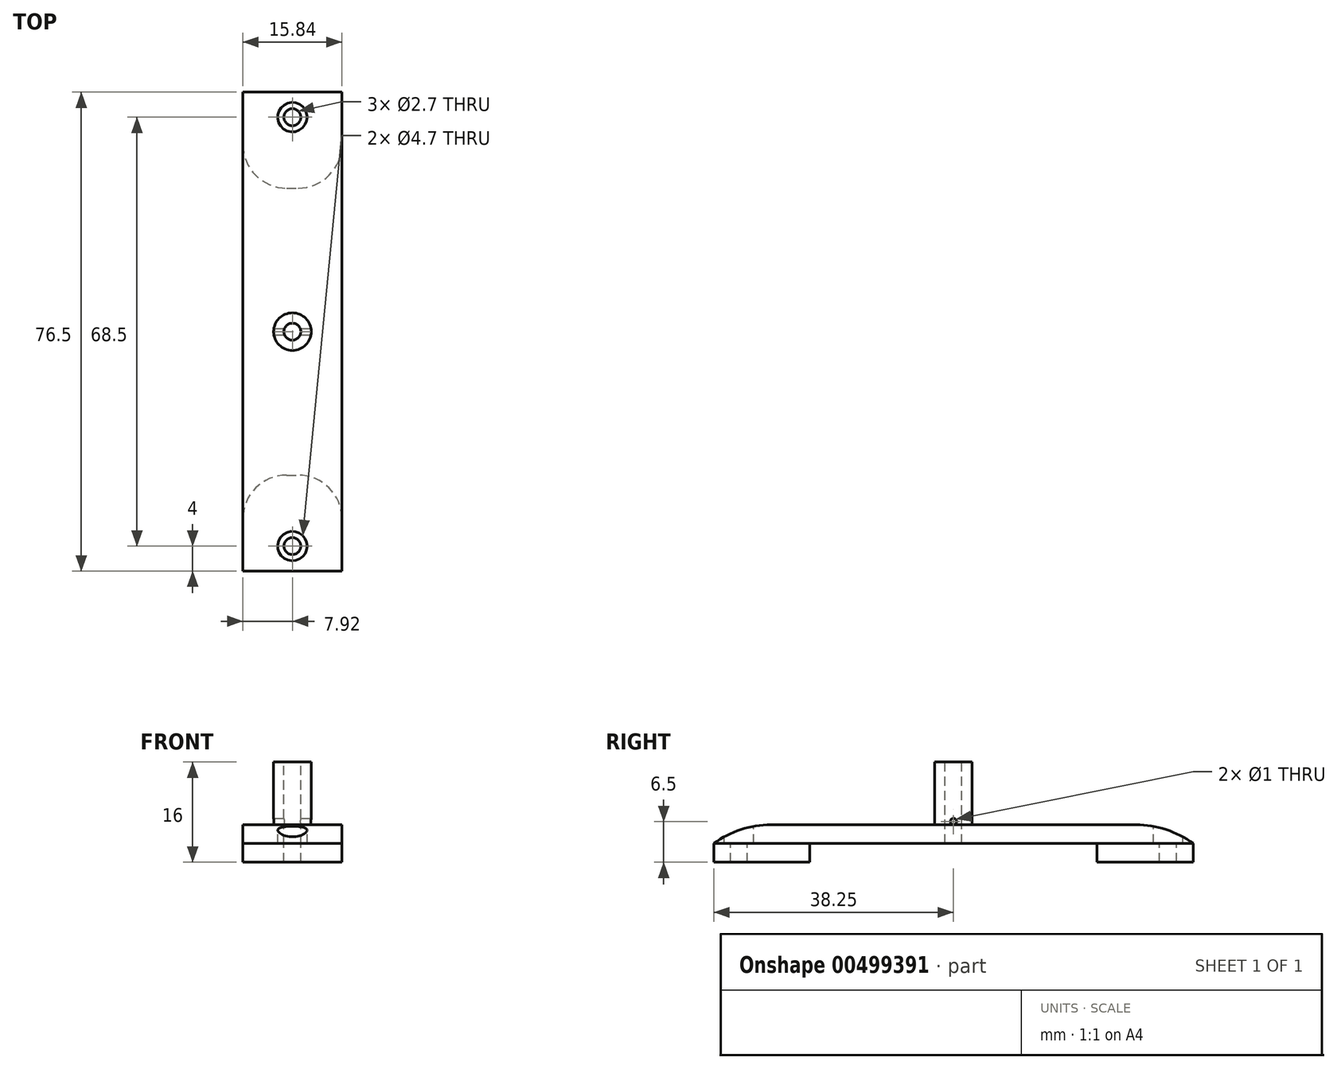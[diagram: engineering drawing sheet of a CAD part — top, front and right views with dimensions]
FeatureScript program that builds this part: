
annotation { "Feature Type Name" : "Feature", "Feature Type Description" : "" }
export const myFeature = defineFeature(function(context is Context, id is Id, definition is map)
    precondition{}
    {
        {
            var Q0;
            Q0=qCreatedBy(makeId("Top.planeOp"),FACE);
            var sketch = newSketch(context, id + "F0", { "sketchPlane" : qUnion([Q0])});
            skLineSegment(sketch, "E0.bottom", {"start": v(-7.92, 38.25) * mm, "end": v(7.91, 38.25) * mm});
            skLineSegment(sketch, "E0.top", {"start": v(-7.92, 22.92) * mm, "end": v(7.91, 22.92) * mm});
            skLineSegment(sketch, "E0.left", {"start": v(-7.92, 22.92) * mm, "end": v(-7.92, 38.25) * mm});
            skLineSegment(sketch, "E0.right", {"start": v(7.91, 22.92) * mm, "end": v(7.91, 38.25) * mm});
            skPoint(sketch, "E0.middle", {"position": v(0, 30.59) * mm});
            skLineSegment(sketch, "E1.bottom", {"start": v(-7.92, -38.25) * mm, "end": v(7.91, -38.25) * mm});
            skLineSegment(sketch, "E1.top", {"start": v(-7.92, -22.92) * mm, "end": v(7.91, -22.92) * mm});
            skLineSegment(sketch, "E1.left", {"start": v(-7.91, -38.25) * mm, "end": v(-7.91, -22.92) * mm});
            skLineSegment(sketch, "E1.right", {"start": v(7.92, -38.25) * mm, "end": v(7.92, -22.92) * mm});
            skPoint(sketch, "E1.middle", {"position": v(0, -30.58) * mm});
            skSolve(sketch);
        }
        {
            var Q0;
            Q0=makeQuery(id+"F0.imprint","IMPRINT",FACE,{"disambiguationData":[TD([[makeQuery(id+"F0.imprint","IMPRINT",EDGE,{"derivedFrom":sQuery(id+"F0.wireOp",EDGE,"E0.bottom")}),-1.0]])]});
            var Q1;
            Q1=makeQuery(id+"F0.imprint","IMPRINT",FACE,{"disambiguationData":[TD([[makeQuery(id+"F0.imprint","IMPRINT",EDGE,{"derivedFrom":sQuery(id+"F0.wireOp",EDGE,"E1.bottom")}),1.0]])]});
            extrude(context, id + "F1", {"entities" : qUnion([Q0, Q1]), "depth" : 3 * mm});
        }
        {
            var Q0;
            Q0=makeQuery(id+"F1.opExtrude","SWEPT_EDGE",EDGE,{"disambiguationData":[OSD([sQuery(id+"F0.wireOp",EDGE,"E0.top"),sQuery(id+"F0.wireOp",EDGE,"E0.left")])]});
            var Q1;
            Q1=makeQuery(id+"F1.opExtrude","SWEPT_EDGE",EDGE,{"disambiguationData":[OSD([sQuery(id+"F0.wireOp",EDGE,"E0.top"),sQuery(id+"F0.wireOp",EDGE,"E0.right")])]});
            var Q2;
            Q2=makeQuery(id+"F1.opExtrude","SWEPT_EDGE",EDGE,{"disambiguationData":[OSD([sQuery(id+"F0.wireOp",EDGE,"E1.top"),sQuery(id+"F0.wireOp",EDGE,"E1.left")])]});
            var Q3;
            Q3=makeQuery(id+"F1.opExtrude","SWEPT_EDGE",EDGE,{"disambiguationData":[OSD([sQuery(id+"F0.wireOp",EDGE,"E1.top"),sQuery(id+"F0.wireOp",EDGE,"E1.right")])]});
            fillet(context, id + "F2", {"entities" : qUnion([Q0, Q1, Q2, Q3]), "radius" : 7 * mm, "tangentPropagation" : true, "allowEdgeOverflow" : false});
        }
        {
            var Q0;
            Q0=makeQuery(id+"F1.opExtrude","CAP_EDGE",EDGE,{"disambiguationData":[OSD([sQuery(id+"F0.wireOp",EDGE,"E1.bottom")])],"isStart":false});
            cPoint(context, id + "F3", {"entities" : qUnion([Q0]), "parameter" : 0.5});
        }
        {
            var Q0;
            Q0=makeQuery(id+"F1.opExtrude","CAP_EDGE",EDGE,{"disambiguationData":[OSD([sQuery(id+"F0.wireOp",EDGE,"E0.bottom")])],"isStart":false});
            var Q1;
            Q1 = qCreatedBy(id + "F3" ,VERTEX);
            cPlane(context, id + "F4", {"entities" : qUnion([Q0, Q1]), "cplaneType" : CPlaneType.LINE_ANGLE, "offset" : 25 * mm, "angle" : 0 * degree, "width" : 150 * mm, "height" : 150 * mm});
        }
        {
            var Q0;
            Q0=qCreatedBy(id+"F4.planeOp",FACE);
            var sketch = newSketch(context, id + "F5", { "sketchPlane" : qUnion([Q0])});
            skLineSegment(sketch, "E2.bottom", {"start": v(-7.91, 38.25) * mm, "end": v(7.92, 38.25) * mm});
            skLineSegment(sketch, "E2.top", {"start": v(-7.92, -38.25) * mm, "end": v(7.91, -38.25) * mm});
            skLineSegment(sketch, "E2.left", {"start": v(-7.91, 38.25) * mm, "end": v(-7.92, -38.25) * mm});
            skLineSegment(sketch, "E2.right", {"start": v(7.92, 38.25) * mm, "end": v(7.91, -38.25) * mm});
            skPoint(sketch, "E2.middle", {"position": v(0, 0) * mm});
            skSolve(sketch);
        }
        {
            var Q0;
            Q0 = qSketchRegion(id + "F5", true);
            extrude(context, id + "F6", {"entities" : qUnion([Q0]), "oppositeDirection" : true, "depth" : 3 * mm});
        }
        {
            var Q0;
            Q0=makeQuery(id+"F6.opExtrude","CAP_EDGE",EDGE,{"disambiguationData":[OSD([sQuery(id+"F5.wireOp",EDGE,"E2.top")])],"isStart":false});
            var Q1;
            Q1=makeQuery(id+"F6.opExtrude","CAP_EDGE",EDGE,{"disambiguationData":[OSD([sQuery(id+"F5.wireOp",EDGE,"E2.bottom")])],"isStart":false});
            fillet(context, id + "F7", {"entities" : qUnion([Q0, Q1]), "radius" : 15.36 * mm, "allowEdgeOverflow" : false});
        }
        {
            var Q0;
            Q0=makeQuery(id+"F6.opExtrude","CAP_EDGE",EDGE,{"disambiguationData":[OSD([sQuery(id+"F5.wireOp",EDGE,"E2.left")])],"isStart":false});
            cPoint(context, id + "F8", {"entities" : qUnion([Q0]), "parameter" : 0.5});
        }
        {
            var Q0;
            Q0=makeQuery(id+"F6.opExtrude","CAP_EDGE",EDGE,{"disambiguationData":[OSD([sQuery(id+"F5.wireOp",EDGE,"E2.right")])],"isStart":false});
            var Q1;
            Q1 = qCreatedBy(id + "F8" ,VERTEX);
            cPlane(context, id + "F9", {"entities" : qUnion([Q0, Q1]), "cplaneType" : CPlaneType.LINE_ANGLE, "offset" : 25 * mm, "angle" : 0 * degree, "width" : 150 * mm, "height" : 150 * mm});
        }
        {
            var Q0;
            Q0=qCreatedBy(id+"F9.planeOp",FACE);
            var sketch = newSketch(context, id + "F10", { "sketchPlane" : qUnion([Q0])});
            skCircle(sketch, "E3", {"center": v(0, 34.25) * mm, "radius": 1.5 * mm});
            skCircle(sketch, "E4", {"center": v(0, -34.25) * mm, "radius": 1.5 * mm});
            skSolve(sketch);
        }
        {
            var Q0;
            Q0=sQuery(id+"F10.wireOp",VERTEX,"E3.center");
            var Q1;
            Q1=sQuery(id+"F10.wireOp",VERTEX,"E4.center");
            var Q2;
            Q2=makeQuery(id+"F1.opExtrude","SWEPT_BODY",BODY,{"disambiguationData":[OSD([sQuery(id+"F0.wireOp",EDGE,"E0.bottom"),sQuery(id+"F0.wireOp",EDGE,"E0.top"),sQuery(id+"F0.wireOp",EDGE,"E0.left"),sQuery(id+"F0.wireOp",EDGE,"E0.right")])]});
            var Q3;
            Q3=makeQuery(id+"F6.opExtrude","SWEPT_BODY",BODY,{"disambiguationData":[OSD([sQuery(id+"F5.wireOp",EDGE,"E2.bottom"),sQuery(id+"F5.wireOp",EDGE,"E2.top"),sQuery(id+"F5.wireOp",EDGE,"E2.left"),sQuery(id+"F5.wireOp",EDGE,"E2.right")])]});
            var Q4;
            Q4=makeQuery(id+"F1.opExtrude","SWEPT_BODY",BODY,{"disambiguationData":[OSD([sQuery(id+"F0.wireOp",EDGE,"E1.bottom"),sQuery(id+"F0.wireOp",EDGE,"E1.top"),sQuery(id+"F0.wireOp",EDGE,"E1.left"),sQuery(id+"F0.wireOp",EDGE,"E1.right")])]});
            hole(context, id + "F11", {"style" : HoleStyle.C_BORE, "endStyle" : HoleEndStyle.BLIND, "holeDiameter" : 2.7 * mm, "cBoreDiameter" : 4.7 * mm, "cBoreDepth" : 3 * mm, "holeDepth" : 10 * mm, "isTappedThrough" : true, "tappedDepth" : 12 * mm, "tapClearance" : 3, "startFromSketch" : true, "locations" : qUnion([Q0, Q1]), "scope" : qUnion([Q2, Q3, Q4])});
        }
        {
            var Q0;
            Q0=qCreatedBy(id+"F9.planeOp",FACE);
            var sketch = newSketch(context, id + "F12", { "sketchPlane" : qUnion([Q0])});
            skCircle(sketch, "E5", {"center": v(0, 0) * mm, "radius": 3 * mm});
            skSolve(sketch);
        }
        {
            var Q0;
            Q0=makeQuery(id+"F12.imprint","IMPRINT",FACE,{"disambiguationData":[TD([[makeQuery(id+"F12.imprint","IMPRINT",EDGE,{"derivedFrom":sQuery(id+"F12.wireOp",EDGE,"E5")}),1.0]])]});
            extrude(context, id + "F13", {"entities" : qUnion([Q0]), "operationType" : NewBodyOperationType.ADD, "depth" : 10 * mm});
        }
        {
            var Q0;
            Q0=makeQuery(id+"F13.opExtrude","CAP_FACE",FACE,{"disambiguationData":[OSD([sQuery(id+"F12.wireOp",EDGE,"E5")])],"isStart":false});
            var sketch = newSketch(context, id + "F14", { "sketchPlane" : qUnion([Q0])});
            skCircle(sketch, "E6", {"center": v(0, 0) * mm, "radius": 1.52 * mm});
            skSolve(sketch);
        }
        {
            var Q0;
            Q0=sQuery(id+"F14.wireOp",VERTEX,"E6.center");
            var Q1;
            Q1=makeQuery(id+"F6.opExtrude","SWEPT_BODY",BODY,{"disambiguationData":[OSD([sQuery(id+"F5.wireOp",EDGE,"E2.bottom"),sQuery(id+"F5.wireOp",EDGE,"E2.top"),sQuery(id+"F5.wireOp",EDGE,"E2.left"),sQuery(id+"F5.wireOp",EDGE,"E2.right")])]});
            hole(context, id + "F15", {"style" : HoleStyle.SIMPLE, "endStyle" : HoleEndStyle.BLIND, "holeDiameter" : 2.7 * mm, "holeDepth" : 20 * mm, "isTappedThrough" : true, "tappedDepth" : 12 * mm, "tapClearance" : 3, "startFromSketch" : true, "locations" : qUnion([Q0]), "scope" : qUnion([Q1])});
        }
        {
            var Q0;
            Q0=makeQuery(id+"F6.opExtrude","SWEPT_FACE",FACE,{"disambiguationData":[OSD([sQuery(id+"F5.wireOp",EDGE,"E2.right")])]});
            var sketch = newSketch(context, id + "F16", { "sketchPlane" : qUnion([Q0])});
            skCircle(sketch, "E7", {"center": v(0, 6.5) * mm, "radius": 0.5 * mm});
            skSolve(sketch);
        }
        {
            var Q0;
            Q0=sQuery(id+"F16.wireOp",VERTEX,"E7.center");
            var Q1;
            Q1=makeQuery(id+"F6.opExtrude","SWEPT_BODY",BODY,{"disambiguationData":[OSD([sQuery(id+"F5.wireOp",EDGE,"E2.bottom"),sQuery(id+"F5.wireOp",EDGE,"E2.top"),sQuery(id+"F5.wireOp",EDGE,"E2.left"),sQuery(id+"F5.wireOp",EDGE,"E2.right")])]});
            hole(context, id + "F17", {"style" : HoleStyle.SIMPLE, "endStyle" : HoleEndStyle.THROUGH, "holeDiameter" : 1 * mm, "isTappedThrough" : true, "tappedDepth" : 12 * mm, "tapClearance" : 3, "startFromSketch" : true, "locations" : qUnion([Q0]), "scope" : qUnion([Q1])});
        }
    });
